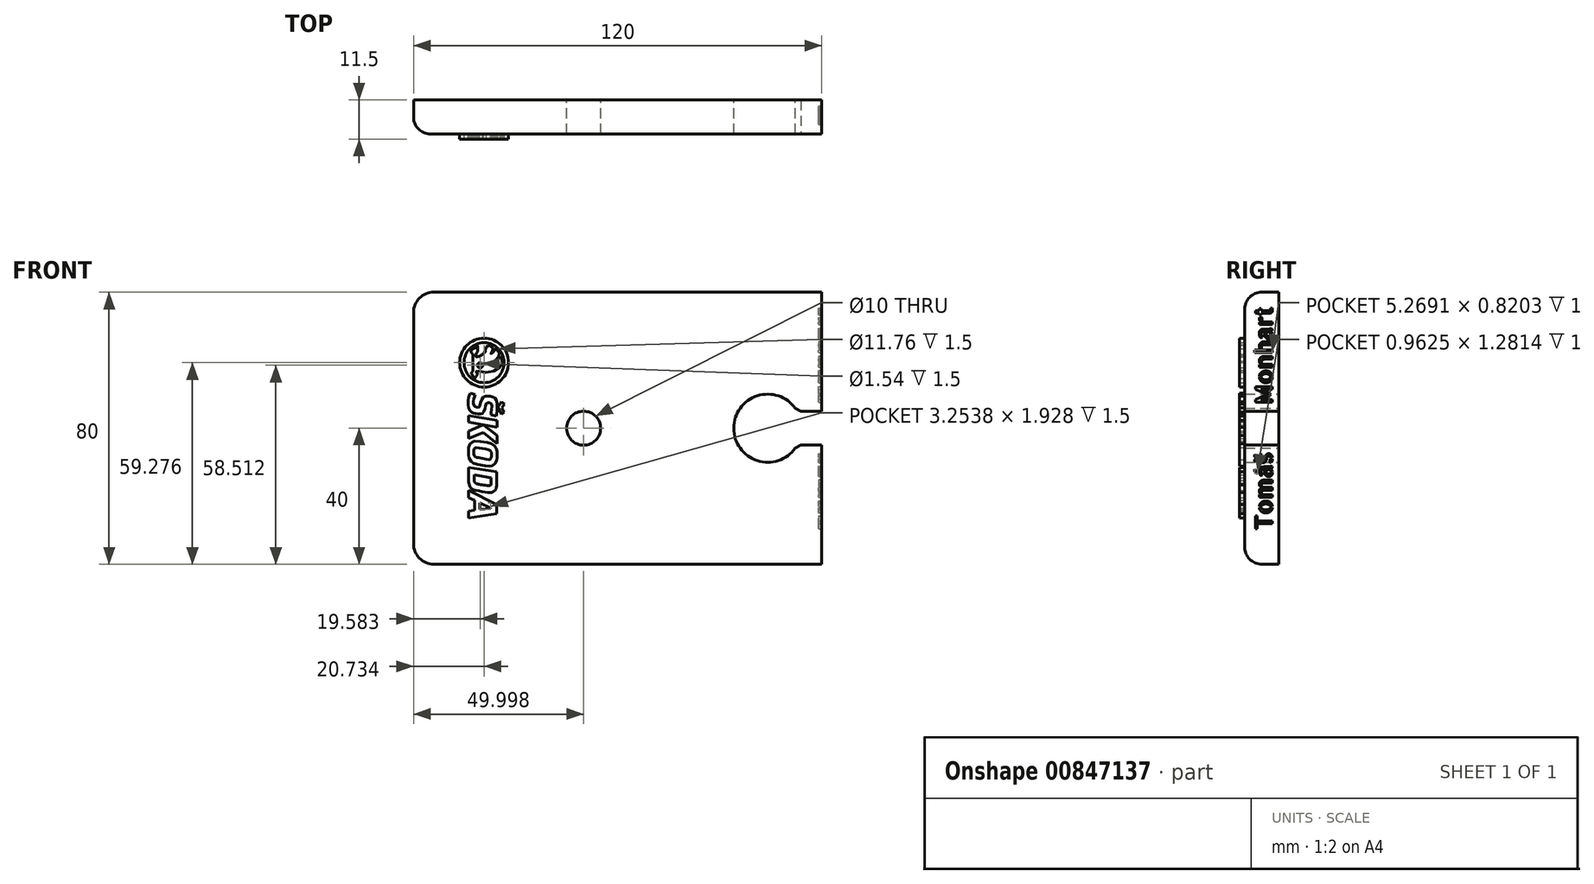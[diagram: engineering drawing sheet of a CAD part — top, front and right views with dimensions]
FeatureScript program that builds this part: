
annotation { "Feature Type Name" : "Feature", "Feature Type Description" : "" }
export const myFeature = defineFeature(function(context is Context, id is Id, definition is map)
    precondition{}
    {
        {
            var Q0;
            Q0=qCreatedBy(makeId("Front.planeOp"),FACE);
            var sketch = newSketch(context, id + "F0", { "sketchPlane" : qUnion([Q0])});
            skLineSegment(sketch, "E0.bottom", {"start": v(-66.83, 40) * mm, "end": v(53.17, 40) * mm});
            skLineSegment(sketch, "E0.top", {"start": v(-66.83, -40) * mm, "end": v(53.17, -40) * mm});
            skLineSegment(sketch, "E0.left", {"start": v(-66.83, 40) * mm, "end": v(-66.83, -40) * mm});
            skLineSegment(sketch, "E0.right", {"start": v(53.17, 40) * mm, "end": v(53.17, 5) * mm});
            skCircle(sketch, "E1", {"center": v(-16.83, 0) * mm, "radius": 5 * mm});
            skPoint(sketch, "E1.centerSnap0", {"position": v(-66.83, 0) * mm});
            skLineSegment(sketch, "E2.bottom", {"start": v(53.17, 5) * mm, "end": v(47.27, 5) * mm});
            skLineSegment(sketch, "E2.top", {"start": v(53.17, -5) * mm, "end": v(47.27, -5) * mm});
            skCircle(sketch, "E3", {"center": v(37.27, 0) * mm, "radius": 10 * mm});
            skPoint(sketch, "E3.centerSnap0", {"position": v(47.27, 0) * mm});
            skLineSegment(sketch, "E4", {"start": v(47.27, 5) * mm, "end": v(45.93, 5) * mm});
            skLineSegment(sketch, "E5", {"start": v(47.27, -5) * mm, "end": v(45.93, -5) * mm});
            skLineSegment(sketch, "E6.trimOffspring", {"start": v(53.17, -5) * mm, "end": v(53.17, -40) * mm});
            skSolve(sketch);
        }
        {
            var Q0;
            Q0=makeQuery(id+"F0.imprint","IMPRINT",FACE,{"disambiguationData":[TD([[makeQuery(id+"F0.imprint","IMPRINT",EDGE,{"derivedFrom":sQuery(id+"F0.wireOp",EDGE,"E0.bottom")}),-1.0]])]});
            extrude(context, id + "F1", {"entities" : qUnion([Q0]), "depth" : 10 * mm, "offsetDistance" : 25 * mm});
        }
        {
            var Q0;
            Q0=makeQuery(id+"F0.imprint","IMPRINT",FACE,{"disambiguationData":[TD([[makeQuery(id+"F0.imprint","IMPRINT",EDGE,{"derivedFrom":sQuery(id+"F0.wireOp",EDGE,"E1")}),1.0]])]});
            extrude(context, id + "F2", {"entities" : qUnion([Q0]), "operationType" : NewBodyOperationType.REMOVE, "oppositeDirection" : true, "depth" : 23.2 * mm, "offsetDistance" : 25 * mm});
        }
        {
            var Q0;
            Q0=makeQuery(id+"F1.opExtrude","SWEPT_EDGE",EDGE,{"disambiguationData":[OSD([sQuery(id+"F0.wireOp",EDGE,"E0.top"),sQuery(id+"F0.wireOp",EDGE,"E0.left")])]});
            var Q1;
            Q1=makeQuery(id+"F1.opExtrude","SWEPT_EDGE",EDGE,{"disambiguationData":[OSD([sQuery(id+"F0.wireOp",EDGE,"E0.bottom"),sQuery(id+"F0.wireOp",EDGE,"E0.left")])]});
            fillet(context, id + "F3", {"entities" : qUnion([Q0, Q1]), "radius" : 6 * mm, "tangentPropagation" : true, "allowEdgeOverflow" : false});
        }
        {
            var Q0;
            Q0=makeQuery(id+"F1.opExtrude","SWEPT_EDGE",EDGE,{"disambiguationData":[OSD([sQuery(id+"F0.wireOp",EDGE,"E3"),sQuery(id+"F0.wireOp",EDGE,"E5")])]});
            var Q1;
            Q1=makeQuery(id+"F1.opExtrude","SWEPT_EDGE",EDGE,{"disambiguationData":[OSD([sQuery(id+"F0.wireOp",EDGE,"E3"),sQuery(id+"F0.wireOp",EDGE,"E4")])]});
            chamfer(context, id + "F4", {"entities" : qUnion([Q0, Q1]), "width" : 2 * mm, "tangentPropagation" : true});
        }
        {
            var Q0;
            Q0=makeQuery(id+"F1.opExtrude","CAP_EDGE",EDGE,{"disambiguationData":[OSD([sQuery(id+"F0.wireOp",EDGE,"E0.top")])],"isStart":false});
            fillet(context, id + "F5", {"entities" : qUnion([Q0]), "radius" : 5 * mm, "tangentPropagation" : true, "allowEdgeOverflow" : false});
        }
        {
            var Q0;
            Q0=makeQuery(id+"F1.opExtrude","CAP_FACE",FACE,{"disambiguationData":[OSD([sQuery(id+"F0.wireOp",EDGE,"E0.bottom"),sQuery(id+"F0.wireOp",EDGE,"E0.top"),sQuery(id+"F0.wireOp",EDGE,"E0.left"),sQuery(id+"F0.wireOp",EDGE,"E0.right"),sQuery(id+"F0.wireOp",EDGE,"E1"),sQuery(id+"F0.wireOp",EDGE,"E2.bottom"),sQuery(id+"F0.wireOp",EDGE,"E2.top"),sQuery(id+"F0.wireOp",EDGE,"E3"),sQuery(id+"F0.wireOp",EDGE,"E4"),sQuery(id+"F0.wireOp",EDGE,"E5"),sQuery(id+"F0.wireOp",EDGE,"E6.trimOffspring")])],"isStart":false});
            var sketch = newSketch(context, id + "F6", { "sketchPlane" : qUnion([Q0])});
            skLineSegment(sketch, "E7", {"start": v(-50.6, -18.25) * mm, "end": v(-50.6, -20.43) * mm});
            skLineSegment(sketch, "E8", {"start": v(-50.6, -20.43) * mm, "end": v(-48.92, -21.18) * mm});
            skLineSegment(sketch, "E9", {"start": v(-48.92, -21.18) * mm, "end": v(-48.92, -24.13) * mm});
            skLineSegment(sketch, "E10", {"start": v(-48.92, -24.13) * mm, "end": v(-50.6, -24.36) * mm});
            skLineSegment(sketch, "E11", {"start": v(-50.6, -24.36) * mm, "end": v(-50.6, -26.45) * mm});
            skLineSegment(sketch, "E12", {"start": v(-50.6, -26.45) * mm, "end": v(-42.37, -25.09) * mm});
            skLineSegment(sketch, "E13", {"start": v(-42.37, -25.09) * mm, "end": v(-42.37, -22.42) * mm});
            skLineSegment(sketch, "E14", {"start": v(-42.37, -22.42) * mm, "end": v(-50.6, -18.25) * mm});
            skLineSegment(sketch, "E15", {"start": v(-47.4, -21.97) * mm, "end": v(-47.4, -23.9) * mm});
            skLineSegment(sketch, "E16", {"start": v(-47.4, -23.9) * mm, "end": v(-44.14, -23.59) * mm});
            skLineSegment(sketch, "E17", {"start": v(-44.14, -23.59) * mm, "end": v(-44.14, -23.46) * mm});
            skLineSegment(sketch, "E18", {"start": v(-44.14, -23.46) * mm, "end": v(-47.4, -21.97) * mm});
            skLineSegment(sketch, "E19", {"start": v(-50.6, -11.51) * mm, "end": v(-42.37, -12.87) * mm});
            skLineSegment(sketch, "E20", {"start": v(-42.37, -12.87) * mm, "end": v(-42.37, -16.6) * mm});
            skLineSegment(sketch, "E21", {"start": v(-50.6, -11.51) * mm, "end": v(-50.6, -15.3) * mm});
            skLineSegment(sketch, "E22", {"start": v(-48.99, -15.3) * mm, "end": v(-48.99, -13.75) * mm});
            skLineSegment(sketch, "E23", {"start": v(-48.99, -13.75) * mm, "end": v(-44, -14.6) * mm});
            skLineSegment(sketch, "E24", {"start": v(-44, -14.6) * mm, "end": v(-44, -16.17) * mm});
            skLineSegment(sketch, "E25", {"start": v(-50.6, -3.03) * mm, "end": v(-50.6, -0.9) * mm});
            skLineSegment(sketch, "E26", {"start": v(-50.6, -0.9) * mm, "end": v(-46.56, 0.89) * mm});
            skLineSegment(sketch, "E27", {"start": v(-46.56, 0.89) * mm, "end": v(-46.25, 0.89) * mm});
            skLineSegment(sketch, "E28", {"start": v(-46.25, 0.89) * mm, "end": v(-42.3, -2.1) * mm});
            skLineSegment(sketch, "E29", {"start": v(-42.3, -2.1) * mm, "end": v(-42.3, -4.5) * mm});
            skLineSegment(sketch, "E30", {"start": v(-42.3, -4.5) * mm, "end": v(-46.37, -1.3) * mm});
            skLineSegment(sketch, "E31", {"start": v(-46.37, -1.3) * mm, "end": v(-50.6, -3.03) * mm});
            skLineSegment(sketch, "E32", {"start": v(-42.3, 0.26) * mm, "end": v(-50.6, 1.75) * mm});
            skLineSegment(sketch, "E33", {"start": v(-50.6, 1.75) * mm, "end": v(-50.6, 3.68) * mm});
            skLineSegment(sketch, "E34", {"start": v(-50.6, 3.68) * mm, "end": v(-42.3, 2.28) * mm});
            skLineSegment(sketch, "E35", {"start": v(-42.3, 2.28) * mm, "end": v(-42.3, 0.26) * mm});
            skLineSegment(sketch, "E36", {"start": v(-50.17, 10.36) * mm, "end": v(-48.75, 9.97) * mm});
            skLineSegment(sketch, "E37", {"start": v(-44.1, 3.9) * mm, "end": v(-42.55, 3.55) * mm});
            skLineSegment(sketch, "E38", {"start": v(-40.93, 7.73) * mm, "end": v(-42, 6.2) * mm});
            skLineSegment(sketch, "E39", {"start": v(-42, 6.2) * mm, "end": v(-41.01, 4.02) * mm});
            skLineSegment(sketch, "E40", {"start": v(-41.01, 4.02) * mm, "end": v(-40.2, 4.67) * mm});
            skLineSegment(sketch, "E41", {"start": v(-40.2, 4.67) * mm, "end": v(-40.81, 5.98) * mm});
            skLineSegment(sketch, "E42", {"start": v(-40.81, 5.98) * mm, "end": v(-40.15, 7.11) * mm});
            skLineSegment(sketch, "E43", {"start": v(-40.15, 7.11) * mm, "end": v(-40.93, 7.73) * mm});
            skCircle(sketch, "E44", {"center": v(-46.1, 19.28) * mm, "radius": 7.18 * mm});
            skPoint(sketch, "E44.first.point", {"position": v(-43.84, 26.1) * mm});
            skPoint(sketch, "E44.second.point", {"position": v(-48.34, 12.45) * mm});
            skPoint(sketch, "E44.third.point", {"position": v(-38.92, 18.93) * mm});
            skCircle(sketch, "E45", {"center": v(-46.1, 19.28) * mm, "radius": 5.88 * mm});
            skCircle(sketch, "E46", {"center": v(-47.25, 18.51) * mm, "radius": 0.77 * mm});
            skPoint(sketch, "E46.first.point", {"position": v(-47.06, 19.26) * mm});
            skPoint(sketch, "E46.second.point", {"position": v(-47.4, 17.75) * mm});
            skPoint(sketch, "E46.third.point", {"position": v(-46.48, 18.45) * mm});
            skLineSegment(sketch, "E47", {"start": v(-49.36, 21.39) * mm, "end": v(-49.36, 16.77) * mm});
            skLineSegment(sketch, "E48", {"start": v(-48.46, 21.1) * mm, "end": v(-48.46, 21.76) * mm});
            skFitSpline(sketch, "E49", {"points": [v(-49.36, 16.77) * mm, v(-49.42, 16.63) * mm, v(-49.57, 16.53) * mm, v(-49.82, 16.47) * mm, v(-49.86, 16.44) * mm, v(-49.81, 15.83) * mm, v(-49.02, 14.65) * mm, v(-48.87, 14.63) * mm, v(-48.79, 14.68) * mm, v(-48.22, 15.4) * mm, v(-47.98, 15.83) * mm, v(-47.98, 16.27) * mm, v(-48.05, 16.39) * mm, v(-48.27, 16.5) * mm, v(-48.38, 16.53) * mm, v(-48.45, 16.77) * mm, v(-48.46, 17.04) * mm, v(-48.38, 17.08) * mm, v(-48.02, 16.88) * mm, v(-46.82, 16.51) * mm, v(-45.75, 16.4) * mm, v(-44.49, 16.47) * mm, v(-43.31, 16.77) * mm, v(-42.26, 17.28) * mm, v(-41.4, 17.93) * mm, v(-41, 18.35) * mm, v(-40.83, 18.62) * mm, v(-40.71, 19.09) * mm, v(-40.77, 20.02) * mm, v(-40.93, 20.75) * mm, v(-41.06, 21.01) * mm, v(-41.3, 21.08) * mm, v(-41.53, 20.92) * mm, v(-42.38, 19.91) * mm, v(-42.58, 19.74) * mm, v(-42.75, 19.71) * mm, v(-42.88, 19.8) * mm, v(-42.87, 20) * mm, v(-42.65, 20.23) * mm, v(-41.74, 21.15) * mm, v(-41.51, 21.43) * mm, v(-41.44, 21.71) * mm, v(-41.49, 22.05) * mm, v(-41.82, 22.56) * mm, v(-42.25, 23.02) * mm, v(-42.64, 23.33) * mm, v(-42.92, 23.4) * mm, v(-43.12, 22.98) * mm, v(-43.5, 22.25) * mm, v(-43.74, 21.83) * mm, v(-43.88, 21.73) * mm, v(-44.02, 21.75) * mm, v(-44.07, 21.86) * mm, v(-43.9, 22.26) * mm, v(-43.45, 23.17) * mm, v(-43.34, 23.47) * mm, v(-43.35, 23.73) * mm, v(-43.44, 23.94) * mm, v(-44.95, 24.52) * mm, v(-45.33, 24.47) * mm, v(-45.4, 24.24) * mm, v(-45.42, 23.66) * mm, v(-45.75, 22.6) * mm, v(-46.23, 21.95) * mm, v(-46.97, 21.36) * mm, v(-47.55, 21.14) * mm, v(-47.91, 21.06) * mm, v(-48.21, 21.02) * mm, v(-48.4, 21.03) * mm, v(-48.45, 21.03) * mm, v(-48.46, 21.1) * mm], "startDerivative": vector(-5.26, -17.66) * mm, "endDerivative": vector(7.42, 11.72) * mm});
            skPoint(sketch, "E50.9.internal.snap0", {"position": v(-48.46, 21.43) * mm});
            skFitSpline(sketch, "E50", {"points": [v(-49.36, 21.39) * mm, v(-49.36, 21.61) * mm, v(-49.73, 22.14) * mm, v(-49.84, 22.33) * mm, v(-49.86, 23.12) * mm, v(-49.68, 23.18) * mm, v(-49.36, 23.27) * mm, v(-48.95, 23.48) * mm, v(-48.55, 23.82) * mm, v(-48.46, 23.9) * mm, v(-48.34, 24.04) * mm, v(-48.28, 24.2) * mm, v(-48.08, 24.25) * mm, v(-48, 24.11) * mm, v(-47.98, 22.63) * mm, v(-48.03, 22.53) * mm, v(-48.24, 22.2) * mm, v(-48.46, 21.76) * mm], "startDerivative": vector(1.44, 4.04) * mm, "endDerivative": vector(-0.8, -6.37) * mm});
            skFitSpline(sketch, "E51", {"points": [v(-50.17, 10.36) * mm, v(-50.45, 9.66) * mm, v(-50.7, 8.4) * mm, v(-50.63, 6.16) * mm, v(-50.17, 5.07) * mm, v(-49.45, 4.56) * mm, v(-48.8, 4.34) * mm, v(-47.92, 4.15) * mm, v(-46.92, 4.2) * mm, v(-46.45, 4.5) * mm, v(-45.88, 5.55) * mm, v(-45.57, 6.9) * mm, v(-45.3, 7.44) * mm, v(-44.68, 7.51) * mm, v(-44.07, 7.25) * mm, v(-43.83, 6.65) * mm, v(-43.92, 5) * mm, v(-44.1, 3.9) * mm], "startDerivative": vector(-5.73, -12.87) * mm, "endDerivative": vector(-2.93, -15.97) * mm});
            skFitSpline(sketch, "E52", {"points": [v(-42.55, 3.55) * mm, v(-42.45, 3.9) * mm, v(-42.3, 5.18) * mm, v(-42.23, 6.97) * mm, v(-42.45, 8.2) * mm, v(-42.85, 8.83) * mm, v(-43.4, 9.16) * mm, v(-44.1, 9.35) * mm, v(-44.71, 9.43) * mm, v(-45.38, 9.47) * mm, v(-46.06, 9.35) * mm, v(-46.6, 8.9) * mm, v(-46.96, 7.99) * mm, v(-47.27, 6.82) * mm, v(-47.42, 6.43) * mm, v(-47.61, 6.18) * mm, v(-48.36, 6.22) * mm, v(-48.75, 6.34) * mm, v(-48.97, 6.49) * mm, v(-49.13, 6.83) * mm, v(-49.2, 7.5) * mm, v(-49.18, 8.03) * mm, v(-49.08, 8.7) * mm, v(-48.89, 9.43) * mm, v(-48.75, 9.97) * mm], "startDerivative": vector(3.48, 9.47) * mm, "endDerivative": vector(3.38, 13.93) * mm});
            skFitSpline(sketch, "E53", {"points": [v(-42.37, -16.6) * mm, v(-42.46, -17.32) * mm, v(-42.72, -18.06) * mm, v(-43.36, -18.66) * mm, v(-43.79, -18.89) * mm, v(-44.77, -18.88) * mm, v(-48.21, -18.35) * mm, v(-49.4, -18.01) * mm, v(-50.15, -17.34) * mm, v(-50.5, -16.43) * mm, v(-50.6, -15.3) * mm], "startDerivative": vector(-0.84, -8.73) * mm, "endDerivative": vector(-0.11, 12.43) * mm});
            skFitSpline(sketch, "E54", {"points": [v(-44, -16.17) * mm, v(-44.08, -16.5) * mm, v(-44.28, -16.83) * mm, v(-44.88, -16.9) * mm, v(-47, -16.59) * mm, v(-47.96, -16.42) * mm, v(-48.33, -16.33) * mm, v(-48.54, -16.23) * mm, v(-48.8, -16) * mm, v(-48.97, -15.69) * mm, v(-48.99, -15.3) * mm], "startDerivative": vector(-0.74, -3.95) * mm, "endDerivative": vector(0.15, 4.68) * mm});
            skFitSpline(sketch, "E55", {"points": [v(-43.86, -7.7) * mm, v(-43.9, -8.37) * mm, v(-44.1, -8.87) * mm, v(-44.48, -9.16) * mm, v(-45.26, -9.12) * mm, v(-48.01, -8.62) * mm, v(-48.51, -8.52) * mm, v(-48.85, -8.26) * mm, v(-49.09, -7.72) * mm, v(-49.1, -7.18) * mm, v(-49.07, -6.43) * mm, v(-48.95, -6.08) * mm, v(-48.76, -5.82) * mm, v(-48.3, -5.7) * mm, v(-46.54, -6.02) * mm, v(-44.62, -6.36) * mm, v(-44.03, -6.95) * mm, v(-43.86, -7.7) * mm]});
            skFitSpline(sketch, "E56", {"points": [v(-42.21, -7.69) * mm, v(-42.27, -8.63) * mm, v(-42.38, -9.3) * mm, v(-42.75, -10.18) * mm, v(-43.44, -10.9) * mm, v(-44.04, -11.17) * mm, v(-45.07, -11.12) * mm, v(-48.83, -10.45) * mm, v(-49.52, -10.09) * mm, v(-50.08, -9.57) * mm, v(-50.59, -8.4) * mm, v(-50.7, -7.78) * mm, v(-50.67, -6.69) * mm, v(-50.6, -5.18) * mm, v(-49.93, -4.36) * mm, v(-49.33, -3.91) * mm, v(-48.56, -3.8) * mm, v(-45.1, -4.23) * mm, v(-43.59, -4.7) * mm, v(-42.81, -5.42) * mm, v(-42.41, -6.3) * mm, v(-42.25, -7.07) * mm, v(-42.21, -7.69) * mm]});
            skSolve(sketch);
        }
        {
            var Q0;
            Q0=makeQuery(id+"F6.imprint","IMPRINT",FACE,{"disambiguationData":[TD([[makeQuery(id+"F6.imprint","IMPRINT",EDGE,{"derivedFrom":sQuery(id+"F6.wireOp",EDGE,"E46")}),-1.0]])]});
            var Q1;
            Q1=makeQuery(id+"F6.imprint","IMPRINT",FACE,{"disambiguationData":[TD([[makeQuery(id+"F6.imprint","IMPRINT",EDGE,{"derivedFrom":sQuery(id+"F6.wireOp",EDGE,"E44")}),1.0]])]});
            var Q2;
            Q2=makeQuery(id+"F6.imprint","IMPRINT",FACE,{"disambiguationData":[TD([[makeQuery(id+"F6.imprint","IMPRINT",EDGE,{"derivedFrom":sQuery(id+"F6.wireOp",EDGE,"E36")}),-1.0]])]});
            var Q3;
            Q3=makeQuery(id+"F6.imprint","IMPRINT",FACE,{"disambiguationData":[TD([[makeQuery(id+"F6.imprint","IMPRINT",EDGE,{"derivedFrom":sQuery(id+"F6.wireOp",EDGE,"E38")}),1.0]])]});
            var Q4;
            Q4=makeQuery(id+"F6.imprint","IMPRINT",FACE,{"disambiguationData":[TD([[makeQuery(id+"F6.imprint","IMPRINT",EDGE,{"derivedFrom":sQuery(id+"F6.wireOp",EDGE,"E32")}),-1.0]])]});
            var Q5;
            Q5=makeQuery(id+"F6.imprint","IMPRINT",FACE,{"disambiguationData":[TD([[makeQuery(id+"F6.imprint","IMPRINT",EDGE,{"derivedFrom":sQuery(id+"F6.wireOp",EDGE,"E25")}),-1.0]])]});
            var Q6;
            Q6=makeQuery(id+"F6.imprint","IMPRINT",FACE,{"disambiguationData":[TD([[makeQuery(id+"F6.imprint","IMPRINT",EDGE,{"derivedFrom":sQuery(id+"F6.wireOp",EDGE,"E55")}),1.0]])]});
            var Q7;
            Q7=makeQuery(id+"F6.imprint","IMPRINT",FACE,{"disambiguationData":[TD([[makeQuery(id+"F6.imprint","IMPRINT",EDGE,{"derivedFrom":sQuery(id+"F6.wireOp",EDGE,"E19")}),-1.0]])]});
            var Q8;
            Q8=makeQuery(id+"F6.imprint","IMPRINT",FACE,{"disambiguationData":[TD([[makeQuery(id+"F6.imprint","IMPRINT",EDGE,{"derivedFrom":sQuery(id+"F6.wireOp",EDGE,"E7")}),1.0]])]});
            extrude(context, id + "F7", {"entities" : qUnion([Q0, Q1, Q2, Q3, Q4, Q5, Q6, Q7, Q8]), "operationType" : NewBodyOperationType.ADD, "depth" : 1.5 * mm, "offsetDistance" : 25 * mm});
        }
        {
            var Q0;
            Q0=makeQuery(id+"F1.opExtrude","SWEPT_FACE",FACE,{"disambiguationData":[OSD([sQuery(id+"F0.wireOp",EDGE,"E6.trimOffspring")])]});
            var sketch = newSketch(context, id + "F8", { "sketchPlane" : qUnion([Q0])});
            skText(sketch, "E57", { "text": "Tomáš", "fontName": "AllertaStencil-Regular.ttf"});
            skText(sketch, "E58", { "text": "Monhart", "fontName": "AllertaStencil-Regular.ttf"});
            const initialGuessF8  = {"E57": [-0.00188, -0.0299, 0, 1, 0.005], "E58": [-0.00188, 0.007, 0, 1, 0.005]};
            skSetInitialGuess(sketch, initialGuessF8);
            skSolve(sketch);
        }
        {
            var Q0;
            Q0 = qSketchRegion(id + "F8", true);
            extrude(context, id + "F9", {"entities" : qUnion([Q0]), "operationType" : NewBodyOperationType.REMOVE, "oppositeDirection" : true, "depth" : 1 * mm, "offsetDistance" : 25 * mm});
        }
    });
